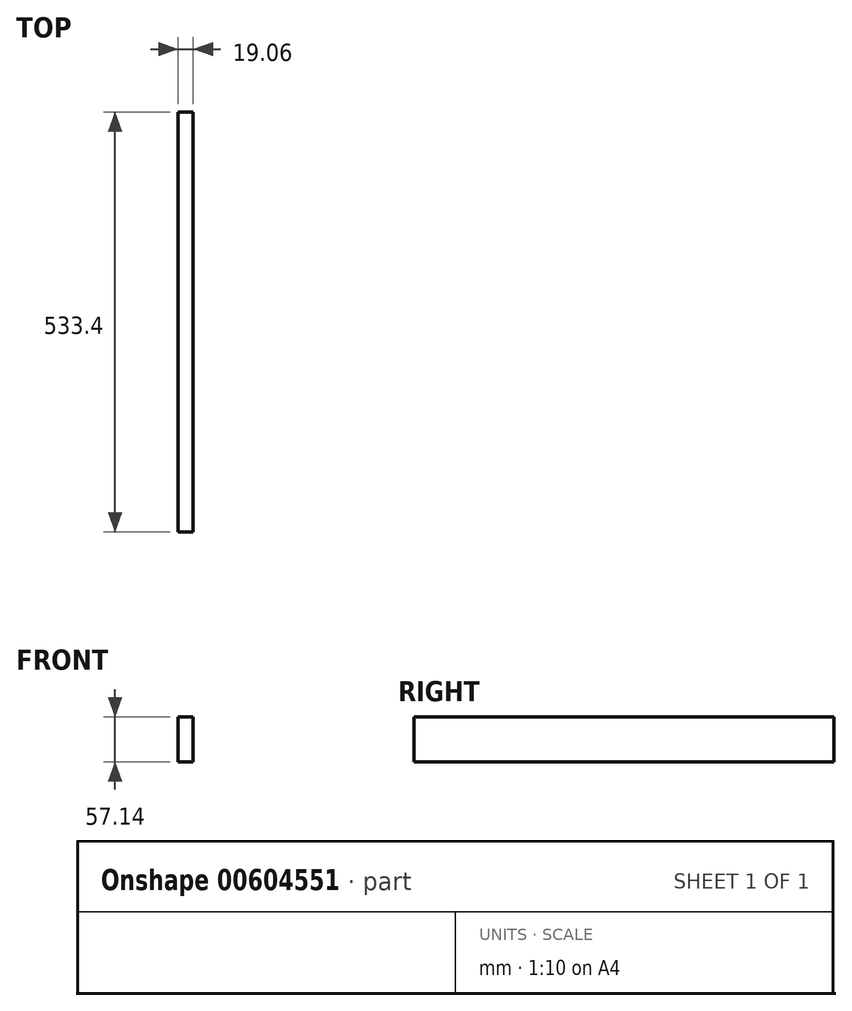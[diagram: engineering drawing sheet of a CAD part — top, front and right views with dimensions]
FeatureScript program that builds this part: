
annotation { "Feature Type Name" : "Feature", "Feature Type Description" : "" }
export const myFeature = defineFeature(function(context is Context, id is Id, definition is map)
    precondition{}
    {
        {
            var Q0;
            Q0=qCreatedBy(makeId("Front.planeOp"),FACE);
            var sketch = newSketch(context, id + "F0", { "sketchPlane" : qUnion([Q0])});
            skLineSegment(sketch, "E0.bottom", {"start": v(9.53, 28.58) * mm, "end": v(-9.52, 28.58) * mm});
            skLineSegment(sketch, "E0.top", {"start": v(9.52, -28.58) * mm, "end": v(-9.53, -28.58) * mm});
            skLineSegment(sketch, "E0.left", {"start": v(9.53, 28.58) * mm, "end": v(9.52, -28.58) * mm});
            skLineSegment(sketch, "E0.right", {"start": v(-9.52, 28.58) * mm, "end": v(-9.53, -28.58) * mm});
            skPoint(sketch, "E0.middle", {"position": v(0, 0) * mm});
            skSolve(sketch);
        }
        {
            var Q0;
            Q0=makeQuery(id+"F0.imprint","IMPRINT",FACE,{"disambiguationData":[TD([[makeQuery(id+"F0.imprint","IMPRINT",EDGE,{"derivedFrom":sQuery(id+"F0.wireOp",EDGE,"E0.bottom")}),1.0]])]});
            extrude(context, id + "F1", {"entities" : qUnion([Q0]), "depth" : 533.4 * mm});
        }
    });
